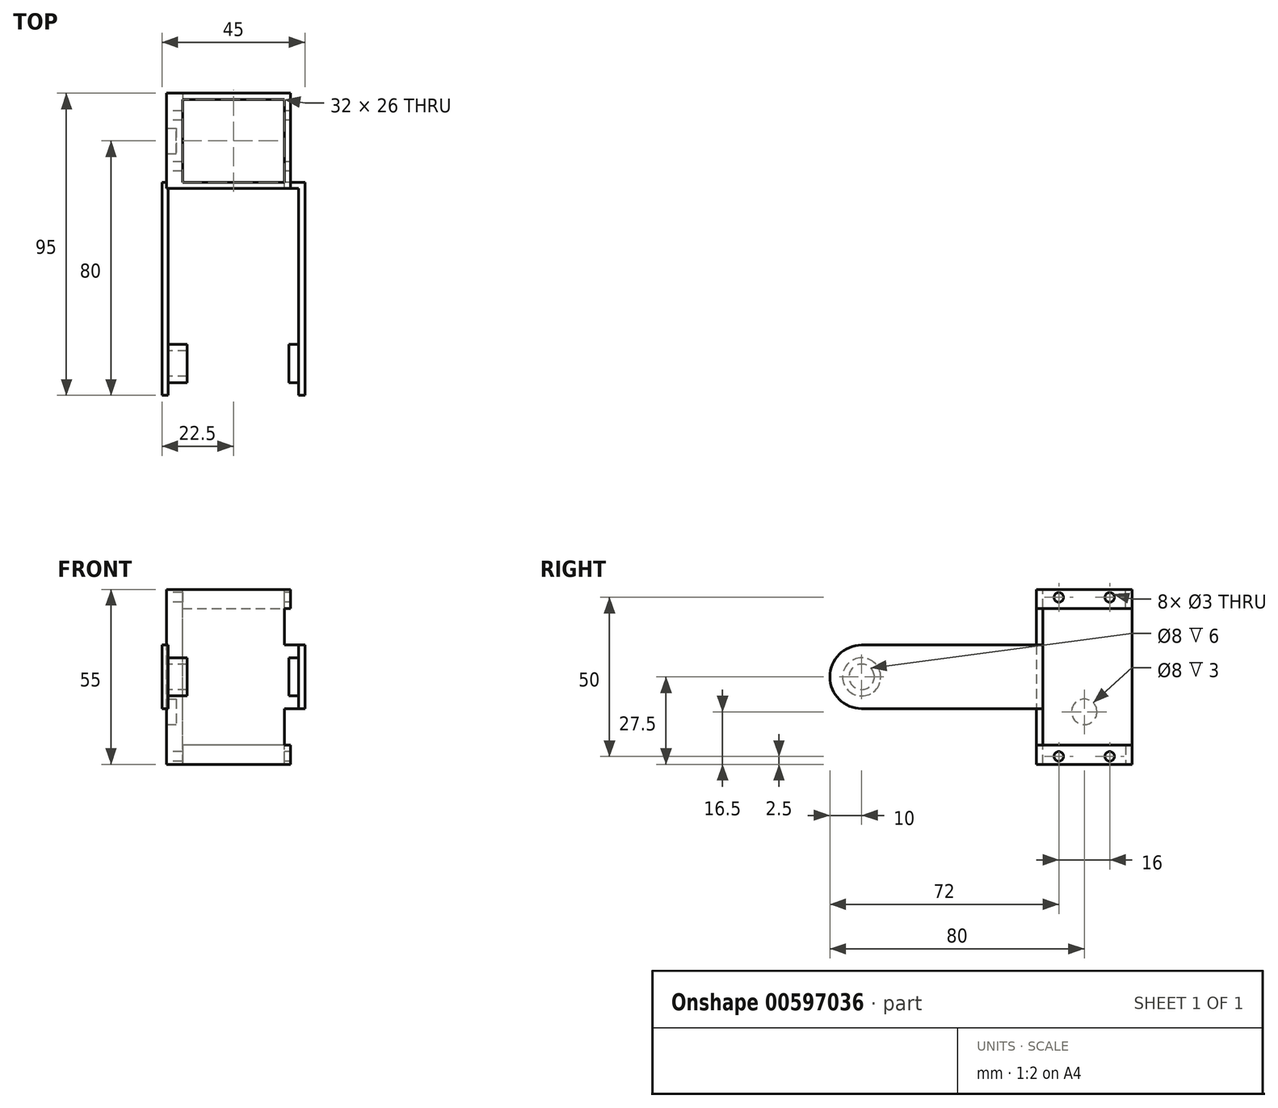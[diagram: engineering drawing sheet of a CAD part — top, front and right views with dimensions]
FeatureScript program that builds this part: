
annotation { "Feature Type Name" : "Feature", "Feature Type Description" : "" }
export const myFeature = defineFeature(function(context is Context, id is Id, definition is map)
    precondition{}
    {
        {
            var Q0;
            Q0=qCreatedBy(makeId("Top.planeOp"),FACE);
            var sketch = newSketch(context, id + "F0", { "sketchPlane" : qUnion([Q0])});
            skLineSegment(sketch, "E0.bottom", {"start": v(22.5, 29.5) * mm, "end": v(-22.5, 29.5) * mm});
            skLineSegment(sketch, "E0.left", {"start": v(22.5, 29.5) * mm, "end": v(22.5, -27.5) * mm});
            skLineSegment(sketch, "E0.right", {"start": v(-22.5, 29.5) * mm, "end": v(-22.5, -27.5) * mm});
            skPoint(sketch, "E0.middle", {"position": v(0, 0) * mm});
            skLineSegment(sketch, "E1.bottom", {"start": v(20.5, 27.5) * mm, "end": v(-20.5, 27.5) * mm});
            skLineSegment(sketch, "E1.left", {"start": v(20.5, 27.5) * mm, "end": v(20.5, -27.5) * mm});
            skLineSegment(sketch, "E1.right", {"start": v(-20.5, 27.5) * mm, "end": v(-20.5, -27.5) * mm});
            skLineSegment(sketch, "E2", {"start": v(-20.5, -27.5) * mm, "end": v(-22.5, -27.5) * mm});
            skLineSegment(sketch, "E3", {"start": v(20.5, -27.5) * mm, "end": v(22.5, -27.5) * mm});
            skPoint(sketch, "E4.orphan", {"position": v(-22.5, -29.5) * mm});
            skPoint(sketch, "E5.orphan", {"position": v(22.5, -29.5) * mm});
            skSolve(sketch);
        }
        {
            var Q0;
            Q0 = qSketchRegion(id + "F0", true);
            extrude(context, id + "F1", {"entities" : qUnion([Q0]), "endBound" : BoundingType.SYMMETRIC, "depth" : 20 * mm, "offsetDistance" : 25.4 * mm});
        }
        {
            var Q0;
            Q0=makeQuery(id+"F1.opExtrude","SWEPT_FACE",FACE,{"disambiguationData":[OSD([sQuery(id+"F0.wireOp",EDGE,"E0.right")])]});
            var sketch = newSketch(context, id + "F2", { "sketchPlane" : qUnion([Q0])});
            skCircle(sketch, "E6", {"center": v(27.5, 0) * mm, "radius": 10 * mm});
            skSolve(sketch);
        }
        {
            var Q0;
            Q0 = qSketchRegion(id + "F2", true);
            extrude(context, id + "F3", {"entities" : qUnion([Q0]), "operationType" : NewBodyOperationType.ADD, "oppositeDirection" : true, "depth" : 2 * mm, "offsetDistance" : 25.4 * mm});
        }
        {
            var Q0;
            Q0=makeQuery(id+"F1.opExtrude","SWEPT_FACE",FACE,{"disambiguationData":[OSD([sQuery(id+"F0.wireOp",EDGE,"E1.left")])]});
            var sketch = newSketch(context, id + "F4", { "sketchPlane" : qUnion([Q0])});
            skArc(sketch, "E7", {"start": v(27.5, -10) * mm, "mid": v(37.5, 0) * mm, "end": v(27.5, 10) * mm});
            skLineSegment(sketch, "E8", {"start": v(27.5, -10) * mm, "end": v(27.5, 10) * mm});
            skSolve(sketch);
        }
        {
            var Q0;
            Q0 = qSketchRegion(id + "F4", true);
            extrude(context, id + "F5", {"entities" : qUnion([Q0]), "operationType" : NewBodyOperationType.ADD, "oppositeDirection" : true, "depth" : 2 * mm, "offsetDistance" : 25.4 * mm});
        }
        {
            var Q0;
            Q0=makeQuery(id+"F3.boolean.opBoolean","MERGE",FACE,{"derivedFrom":[makeQuery(id+"F1.opExtrude","SWEPT_FACE",FACE,{"disambiguationData":[OSD([sQuery(id+"F0.wireOp",EDGE,"E1.right")])]}),makeQuery(id+"F3.opExtrude","CAP_FACE",FACE,{"disambiguationData":[OSD([sQuery(id+"F2.wireOp",EDGE,"E6")])],"isStart":false})]});
            var sketch = newSketch(context, id + "F6", { "sketchPlane" : qUnion([Q0])});
            skCircle(sketch, "E9", {"center": v(-27.5, 0) * mm, "radius": 4 * mm});
            skCircle(sketch, "E10", {"center": v(-27.5, 0) * mm, "radius": 6 * mm});
            skSolve(sketch);
        }
        {
            var Q0;
            Q0=makeQuery(id+"F6.imprint","IMPRINT",FACE,{"disambiguationData":[TD([[makeQuery(id+"F6.imprint","IMPRINT",EDGE,{"derivedFrom":sQuery(id+"F6.wireOp",EDGE,"E9")}),-1.0]])]});
            extrude(context, id + "F7", {"entities" : qUnion([Q0]), "operationType" : NewBodyOperationType.ADD, "depth" : 6 * mm, "offsetDistance" : 25.4 * mm});
        }
        {
            var Q0;
            Q0=makeQuery(id+"F5.boolean.opBoolean","MERGE",FACE,{"derivedFrom":[makeQuery(id+"F1.opExtrude","SWEPT_FACE",FACE,{"disambiguationData":[OSD([sQuery(id+"F0.wireOp",EDGE,"E1.left")])]}),makeQuery(id+"F5.opExtrude","CAP_FACE",FACE,{"disambiguationData":[OSD([sQuery(id+"F4.wireOp",EDGE,"E7"),sQuery(id+"F4.wireOp",EDGE,"E8")])],"isStart":true})]});
            var sketch = newSketch(context, id + "F8", { "sketchPlane" : qUnion([Q0])});
            skCircle(sketch, "E11", {"center": v(27.5, 0) * mm, "radius": 6 * mm});
            skSolve(sketch);
        }
        {
            var Q0;
            Q0 = qSketchRegion(id + "F8", true);
            extrude(context, id + "F9", {"entities" : qUnion([Q0]), "operationType" : NewBodyOperationType.ADD, "depth" : 3 * mm, "offsetDistance" : 25.4 * mm});
        }
        {
            var Q0;
            Q0=makeQuery(id+"F1.opExtrude","SWEPT_FACE",FACE,{"disambiguationData":[OSD([sQuery(id+"F0.wireOp",EDGE,"E1.bottom")])]});
            var sketch = newSketch(context, id + "F10", { "sketchPlane" : qUnion([Q0])});
            skLineSegment(sketch, "E12.bottom", {"start": v(16, -27.5) * mm, "end": v(-16, -27.5) * mm});
            skLineSegment(sketch, "E12.top", {"start": v(16, 27.5) * mm, "end": v(-16, 27.5) * mm});
            skLineSegment(sketch, "E12.left", {"start": v(16, -27.5) * mm, "end": v(16, 27.5) * mm});
            skLineSegment(sketch, "E12.right", {"start": v(-16, -27.5) * mm, "end": v(-16, 27.5) * mm});
            skPoint(sketch, "E12.middle", {"position": v(0, 0) * mm});
            skLineSegment(sketch, "E13", {"start": v(-16, -10) * mm, "end": v(16, -10) * mm});
            skLineSegment(sketch, "E14", {"start": v(-16, 10) * mm, "end": v(16, 10) * mm});
            skSolve(sketch);
        }
        {
            var Q0;
            {var subQ0=sQuery(id+"F10.wireOp",EDGE,"E12.bottom");Q0=makeQuery(id+"F10.imprint","IMPRINT",FACE,{"disambiguationData":[TD([[makeQuery(id+"F10.imprint","IMPRINT",EDGE,{"derivedFrom":subQ0}),-1.0]])]});}
            var Q1;
            {var subQ0=sQuery(id+"F10.wireOp",EDGE,"E12.top");Q1=makeQuery(id+"F10.imprint","IMPRINT",FACE,{"disambiguationData":[TD([[makeQuery(id+"F10.imprint","IMPRINT",EDGE,{"derivedFrom":subQ0}),1.0]])]});}
            extrude(context, id + "F11", {"entities" : qUnion([Q0, Q1]), "operationType" : NewBodyOperationType.ADD, "oppositeDirection" : true, "depth" : 2 * mm, "offsetDistance" : 25.4 * mm});
        }
        {
            var Q0;
            Q0=makeQuery(id+"F11.opExtrude","SWEPT_FACE",FACE,{"disambiguationData":[OSD([sQuery(id+"F10.wireOp",EDGE,"E12.bottom")])]});
            var sketch = newSketch(context, id + "F12", { "sketchPlane" : qUnion([Q0])});
            skLineSegment(sketch, "E15.bottom", {"start": v(18, -27.5) * mm, "end": v(-18, -27.5) * mm});
            skLineSegment(sketch, "E15.top", {"start": v(18, -57.5) * mm, "end": v(-18, -57.5) * mm});
            skLineSegment(sketch, "E15.left", {"start": v(18, -27.5) * mm, "end": v(18, -57.5) * mm});
            skLineSegment(sketch, "E15.right", {"start": v(-18, -27.5) * mm, "end": v(-18, -57.5) * mm});
            skPoint(sketch, "E16.oppositeSnap0", {"position": v(-16, -28.5) * mm});
            skLineSegment(sketch, "E16.top", {"start": v(16, -55.5) * mm, "end": v(-16, -55.5) * mm});
            skLineSegment(sketch, "E16.left", {"start": v(16, -27.5) * mm, "end": v(16, -55.5) * mm});
            skLineSegment(sketch, "E16.right", {"start": v(-16, -19.5) * mm, "end": v(-16, -55.5) * mm});
            skSolve(sketch);
        }
        {
            var Q0;
            Q0=makeQuery(id+"F12.imprint","IMPRINT",FACE,{"disambiguationData":[TD([[makeQuery(id+"F12.imprint","IMPRINT",EDGE,{"derivedFrom":sQuery(id+"F12.wireOp",EDGE,"E15.top")}),-1.0]])]});
            extrude(context, id + "F13", {"entities" : qUnion([Q0]), "operationType" : NewBodyOperationType.ADD, "oppositeDirection" : true, "depth" : 6 * mm, "offsetDistance" : 25.4 * mm});
        }
        {
            var Q0;
            Q0=makeQuery(id+"F11.opExtrude","SWEPT_FACE",FACE,{"disambiguationData":[OSD([sQuery(id+"F10.wireOp",EDGE,"E12.top")])]});
            var sketch = newSketch(context, id + "F14", { "sketchPlane" : qUnion([Q0])});
            skLineSegment(sketch, "E17.top", {"start": v(-16, 55.5) * mm, "end": v(16, 55.5) * mm});
            skLineSegment(sketch, "E17.left", {"start": v(-16, 27.5) * mm, "end": v(-16, 55.5) * mm});
            skLineSegment(sketch, "E17.right", {"start": v(16, 27.5) * mm, "end": v(16, 55.5) * mm});
            skLineSegment(sketch, "E18.bottom", {"start": v(-18, 27.5) * mm, "end": v(-16, 27.5) * mm});
            skLineSegment(sketch, "E18.top", {"start": v(-18, 57.5) * mm, "end": v(18, 57.5) * mm});
            skLineSegment(sketch, "E18.left", {"start": v(-18, 27.5) * mm, "end": v(-18, 57.5) * mm});
            skLineSegment(sketch, "E18.right", {"start": v(18, 27.5) * mm, "end": v(18, 57.5) * mm});
            skLineSegment(sketch, "E19.trimOffspring", {"start": v(16, 27.5) * mm, "end": v(18, 27.5) * mm});
            skSolve(sketch);
        }
        {
            var Q0;
            Q0 = qSketchRegion(id + "F14", true);
            extrude(context, id + "F15", {"entities" : qUnion([Q0]), "operationType" : NewBodyOperationType.ADD, "oppositeDirection" : true, "depth" : 6 * mm, "offsetDistance" : 25.4 * mm});
        }
        {
            var Q0;
            Q0=makeQuery(id+"F15.opExtrude","SWEPT_FACE",FACE,{"disambiguationData":[OSD([sQuery(id+"F14.wireOp",EDGE,"E18.left")])]});
            var sketch = newSketch(context, id + "F16", { "sketchPlane" : qUnion([Q0])});
            skCircle(sketch, "E20", {"center": v(-50.5, 25) * mm, "radius": 1.5 * mm});
            skCircle(sketch, "E21", {"center": v(-34.5, 25) * mm, "radius": 1.5 * mm});
            skSolve(sketch);
        }
        {
            var Q0;
            Q0=makeQuery(id+"F16.imprint","IMPRINT",FACE,{"disambiguationData":[TD([[makeQuery(id+"F16.imprint","IMPRINT",EDGE,{"derivedFrom":sQuery(id+"F16.wireOp",EDGE,"E20")}),1.0]])]});
            var Q1;
            Q1=makeQuery(id+"F16.imprint","IMPRINT",FACE,{"disambiguationData":[TD([[makeQuery(id+"F16.imprint","IMPRINT",EDGE,{"derivedFrom":sQuery(id+"F16.wireOp",EDGE,"E21")}),1.0]])]});
            extrude(context, id + "F17", {"entities" : qUnion([Q0, Q1]), "operationType" : NewBodyOperationType.REMOVE, "oppositeDirection" : true, "depth" : 50.8 * mm, "offsetDistance" : 25.4 * mm});
        }
        {
            var Q0;
            Q0=makeQuery(id+"F13.opExtrude","SWEPT_FACE",FACE,{"disambiguationData":[OSD([sQuery(id+"F12.wireOp",EDGE,"E15.right")])]});
            var sketch = newSketch(context, id + "F18", { "sketchPlane" : qUnion([Q0])});
            skCircle(sketch, "E22", {"center": v(-50.5, -25) * mm, "radius": 1.5 * mm});
            skCircle(sketch, "E23", {"center": v(-34.5, -25) * mm, "radius": 1.5 * mm});
            skSolve(sketch);
        }
        {
            var Q0;
            Q0=makeQuery(id+"F18.imprint","IMPRINT",FACE,{"disambiguationData":[TD([[makeQuery(id+"F18.imprint","IMPRINT",EDGE,{"derivedFrom":sQuery(id+"F18.wireOp",EDGE,"E22")}),1.0]])]});
            var Q1;
            Q1=makeQuery(id+"F18.imprint","IMPRINT",FACE,{"disambiguationData":[TD([[makeQuery(id+"F18.imprint","IMPRINT",EDGE,{"derivedFrom":sQuery(id+"F18.wireOp",EDGE,"E23")}),1.0]])]});
            extrude(context, id + "F19", {"entities" : qUnion([Q0, Q1]), "operationType" : NewBodyOperationType.REMOVE, "oppositeDirection" : true, "depth" : 50.8 * mm, "offsetDistance" : 25.4 * mm});
        }
        {
            var Q0;
            Q0=makeQuery(id+"F15.opExtrude","CAP_FACE",FACE,{"disambiguationData":[OSD([sQuery(id+"F14.wireOp",EDGE,"E17.top"),sQuery(id+"F14.wireOp",EDGE,"E17.left"),sQuery(id+"F14.wireOp",EDGE,"E17.right"),sQuery(id+"F14.wireOp",EDGE,"E18.bottom"),sQuery(id+"F14.wireOp",EDGE,"E18.top"),sQuery(id+"F14.wireOp",EDGE,"E18.left"),sQuery(id+"F14.wireOp",EDGE,"E18.right"),sQuery(id+"F14.wireOp",EDGE,"E19.trimOffspring")])],"isStart":false});
            var sketch = newSketch(context, id + "F20", { "sketchPlane" : qUnion([Q0])});
            skLineSegment(sketch, "E24.bottom", {"start": v(-18, -57.5) * mm, "end": v(-16, -57.5) * mm});
            skLineSegment(sketch, "E24.top", {"start": v(-18, -27.5) * mm, "end": v(-16, -27.5) * mm});
            skLineSegment(sketch, "E24.left", {"start": v(-18, -57.5) * mm, "end": v(-18, -27.5) * mm});
            skLineSegment(sketch, "E24.right", {"start": v(-16, -57.5) * mm, "end": v(-16, -27.5) * mm});
            skSolve(sketch);
        }
        {
            var Q0;
            Q0 = qSketchRegion(id + "F20", true);
            extrude(context, id + "F21", {"entities" : qUnion([Q0]), "operationType" : NewBodyOperationType.ADD, "depth" : 43 * mm, "offsetDistance" : 25.4 * mm});
        }
        {
            var Q0;
            Q0=makeQuery(id+"F21.boolean.opBoolean","MERGE",FACE,{"derivedFrom":[makeQuery(id+"F15.opExtrude","SWEPT_FACE",FACE,{"disambiguationData":[OSD([sQuery(id+"F14.wireOp",EDGE,"E18.left")])]}),makeQuery(id+"F13.opExtrude","SWEPT_FACE",FACE,{"disambiguationData":[OSD([sQuery(id+"F12.wireOp",EDGE,"E15.right")])]}),makeQuery(id+"F21.opExtrude","SWEPT_FACE",FACE,{"disambiguationData":[OSD([sQuery(id+"F20.wireOp",EDGE,"E24.left")])]})]});
            var sketch = newSketch(context, id + "F22", { "sketchPlane" : qUnion([Q0])});
            skCircle(sketch, "E25", {"center": v(-42.5, 11) * mm, "radius": 4 * mm});
            skPoint(sketch, "E25.centerSnap0", {"position": v(-42.5, 27.5) * mm});
            skLineSegment(sketch, "E26", {"start": v(-57.5, 0) * mm, "end": v(-29.5, 0) * mm, "construction": true});
            skCircle(sketch, "E27.MirrorC", {"center": v(-42.5, -11) * mm, "radius": 4 * mm});
            skSolve(sketch);
        }
        {
            var Q0;
            Q0=makeQuery(id+"F22.imprint","IMPRINT",FACE,{"disambiguationData":[TD([[makeQuery(id+"F22.imprint","IMPRINT",EDGE,{"derivedFrom":sQuery(id+"F22.wireOp",EDGE,"E25")}),1.0]])]});
            var Q1;
            Q1=makeQuery(id+"F22.imprint","IMPRINT",FACE,{"disambiguationData":[TD([[makeQuery(id+"F22.imprint","IMPRINT",EDGE,{"derivedFrom":sQuery(id+"F22.wireOp",EDGE,"E27.MirrorC")}),-1.0]])]});
            extrude(context, id + "F23", {"entities" : qUnion([Q0, Q1]), "operationType" : NewBodyOperationType.ADD, "depth" : 3 * mm, "offsetDistance" : 25.4 * mm});
        }
    });
